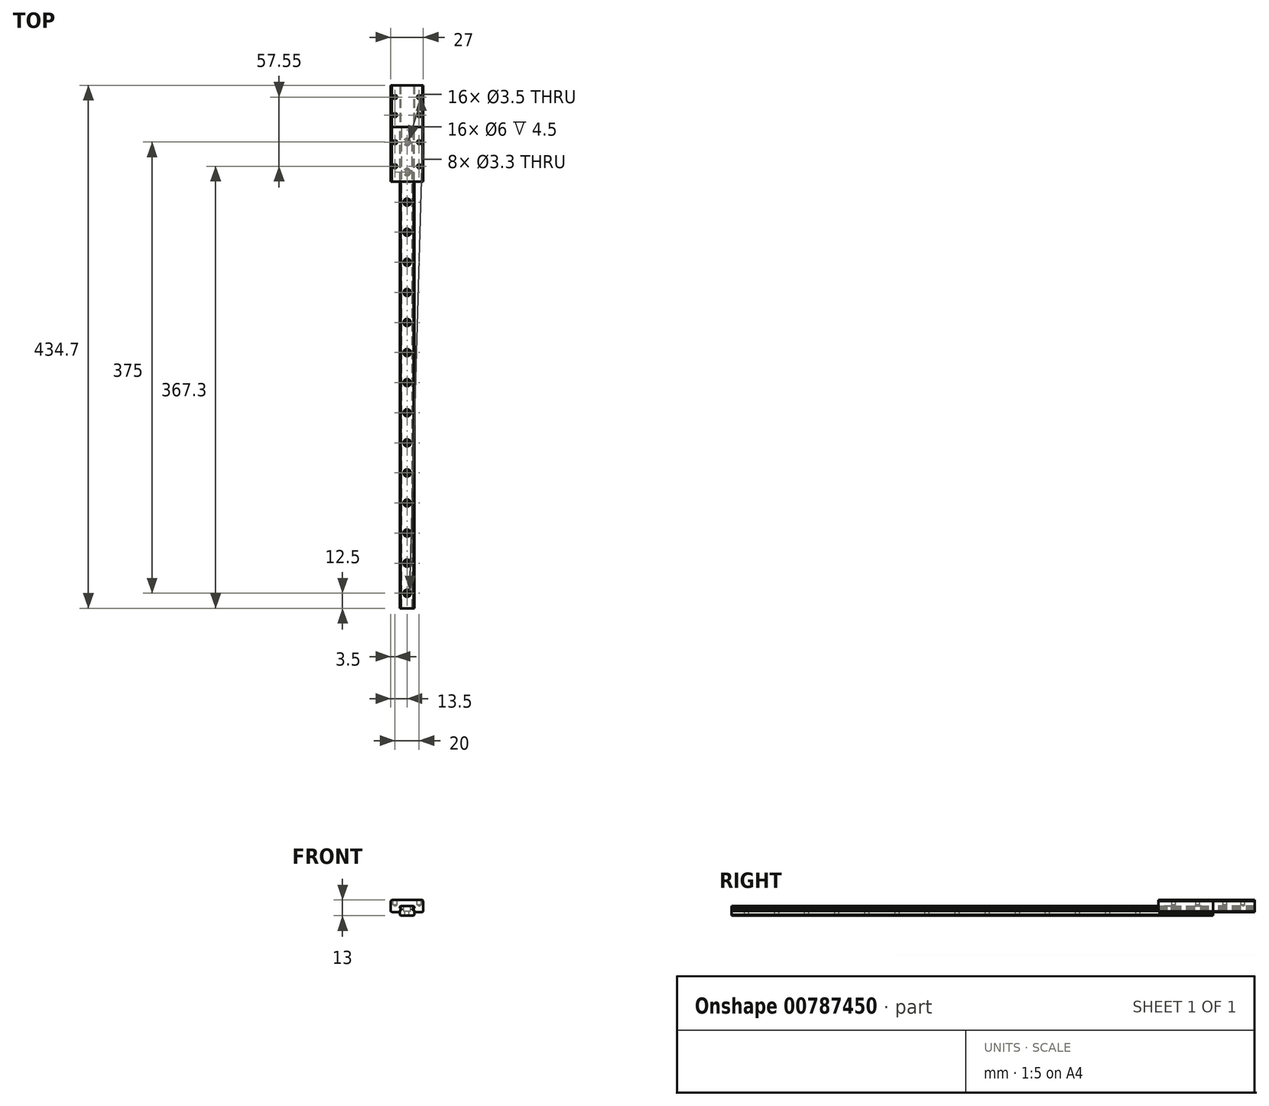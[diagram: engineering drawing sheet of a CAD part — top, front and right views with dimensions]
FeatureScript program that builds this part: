
annotation { "Feature Type Name" : "Feature", "Feature Type Description" : "" }
export const myFeature = defineFeature(function(context is Context, id is Id, definition is map)
    precondition{}
    {
        {
            var Q0;
            Q0=qCreatedBy(makeId("Front.planeOp"),FACE);
            var sketch = newSketch(context, id + "F0", { "sketchPlane" : qUnion([Q0])});
            skLineSegment(sketch, "E0.bottom", {"start": v(5.3, -4) * mm, "end": v(-5.3, -4) * mm});
            skLineSegment(sketch, "E0.top", {"start": v(5.3, 4) * mm, "end": v(-5.3, 4) * mm});
            skLineSegment(sketch, "E0.left", {"start": v(6, -3.3) * mm, "end": v(6, 0.09) * mm});
            skLineSegment(sketch, "E0.right", {"start": v(-6, -3.3) * mm, "end": v(-6, 0.09) * mm});
            skPoint(sketch, "E0.middle", {"position": v(0, 0) * mm});
            skLineSegment(sketch, "E1", {"start": v(0, 12.36) * mm, "end": v(0, -9.73) * mm, "construction": true});
            skLineSegment(sketch, "E2", {"start": v(-6, 2.5) * mm, "end": v(-5.3, 1.8) * mm});
            skLineSegment(sketch, "E3", {"start": v(-5.3, 1.8) * mm, "end": v(-4.3, 1.8) * mm});
            skLineSegment(sketch, "E4", {"start": v(-4.3, 1.8) * mm, "end": v(-4.3, 0.8) * mm});
            skLineSegment(sketch, "E5", {"start": v(-4.3, 0.8) * mm, "end": v(-5.3, 0.8) * mm});
            skLineSegment(sketch, "E6", {"start": v(-5.3, 0.8) * mm, "end": v(-6, 0.09) * mm});
            skLineSegment(sketch, "E7.MirrorCS", {"start": v(4.3, 0.8) * mm, "end": v(5.3, 0.8) * mm});
            skLineSegment(sketch, "E8.MirrorCS", {"start": v(5.3, 0.8) * mm, "end": v(6, 0.09) * mm});
            skLineSegment(sketch, "E9.MirrorCS", {"start": v(4.3, 1.8) * mm, "end": v(4.3, 0.8) * mm});
            skLineSegment(sketch, "E10.MirrorCS", {"start": v(6, 2.5) * mm, "end": v(5.3, 1.8) * mm});
            skLineSegment(sketch, "E11.MirrorCS", {"start": v(5.3, 1.8) * mm, "end": v(4.3, 1.8) * mm});
            skLineSegment(sketch, "E12.trimOffspring", {"start": v(-6, 2.5) * mm, "end": v(-6, 3.3) * mm});
            skLineSegment(sketch, "E13.trimOffspring", {"start": v(6, 2.5) * mm, "end": v(6, 3.3) * mm});
            skLineSegment(sketch, "E14", {"start": v(-6, 3.3) * mm, "end": v(-5.3, 4) * mm});
            skLineSegment(sketch, "E15.MirrorCS", {"start": v(6, 3.3) * mm, "end": v(5.3, 4) * mm});
            skLineSegment(sketch, "E16.MirrorCS", {"start": v(-6, -3.3) * mm, "end": v(-5.3, -4) * mm});
            skLineSegment(sketch, "E17.MirrorCS", {"start": v(6, -3.3) * mm, "end": v(5.3, -4) * mm});
            skPoint(sketch, "E18.orphan", {"position": v(-6, 4) * mm});
            skPoint(sketch, "E19.orphan", {"position": v(6, 4) * mm});
            skPoint(sketch, "E20.orphan", {"position": v(6, -4) * mm});
            skPoint(sketch, "E21.orphan", {"position": v(-6, -4) * mm});
            skSolve(sketch);
        }
        {
            var Q0;
            Q0=makeQuery(id+"F0.imprint","IMPRINT",FACE,{"disambiguationData":[TD([[makeQuery(id+"F0.imprint","IMPRINT",EDGE,{"derivedFrom":sQuery(id+"F0.wireOp",EDGE,"E0.bottom")}),-1.0]])]});
            extrude(context, id + "F1", {"entities" : qUnion([Q0]), "depth" : 400 * mm, "offsetDistance" : 25 * mm});
        }
        {
            var Q0;
            Q0=makeQuery(id+"F1.opExtrude","SWEPT_FACE",FACE,{"disambiguationData":[OSD([sQuery(id+"F0.wireOp",EDGE,"E0.top")])]});
            var sketch = newSketch(context, id + "F2", { "sketchPlane" : qUnion([Q0])});
            skLineSegment(sketch, "E22", {"start": v(0, 4.61) * mm, "end": v(0, -375.08) * mm, "construction": true});
            skCircle(sketch, "E23", {"center": v(0, -12.5) * mm, "radius": 1.75 * mm});
            skCircle(sketch, "E24.1.0.0", {"center": v(0, -37.5) * mm, "radius": 1.75 * mm});
            skCircle(sketch, "E24.2.0.0", {"center": v(0, -62.5) * mm, "radius": 1.75 * mm});
            skCircle(sketch, "E24.3.0.0", {"center": v(0, -87.5) * mm, "radius": 1.75 * mm});
            skCircle(sketch, "E24.4.0.0", {"center": v(0, -112.5) * mm, "radius": 1.75 * mm});
            skCircle(sketch, "E24.5.0.0", {"center": v(0, -137.5) * mm, "radius": 1.75 * mm});
            skCircle(sketch, "E24.6.0.0", {"center": v(0, -162.5) * mm, "radius": 1.75 * mm});
            skCircle(sketch, "E24.7.0.0", {"center": v(0, -187.5) * mm, "radius": 1.75 * mm});
            skCircle(sketch, "E24.8.0.0", {"center": v(0, -212.5) * mm, "radius": 1.75 * mm});
            skLineSegment(sketch, "E24.direction1", {"start": v(0, -12.5) * mm, "end": v(0, -37.5) * mm, "construction": true});
            skCircle(sketch, "E25.0.9.0", {"center": v(0, -237.5) * mm, "radius": 1.75 * mm});
            skCircle(sketch, "E25.0.10.0", {"center": v(0, -262.5) * mm, "radius": 1.75 * mm});
            skCircle(sketch, "E25.0.11.0", {"center": v(0, -287.5) * mm, "radius": 1.75 * mm});
            skCircle(sketch, "E25.0.12.0", {"center": v(0, -312.5) * mm, "radius": 1.75 * mm});
            skCircle(sketch, "E25.0.13.0", {"center": v(0, -337.5) * mm, "radius": 1.75 * mm});
            skCircle(sketch, "E26.0.14.0", {"center": v(0, -362.5) * mm, "radius": 1.75 * mm});
            skCircle(sketch, "E26.0.15.0", {"center": v(0, -387.5) * mm, "radius": 1.75 * mm});
            skSolve(sketch);
        }
        {
            var Q0;
            Q0=qSketchRegion(id+"F2",true);
            extrude(context, id + "F3", {"entities" : qUnion([Q0]), "operationType" : NewBodyOperationType.REMOVE, "endBound" : BoundingType.THROUGH_ALL, "oppositeDirection" : true, "depth" : 25 * mm, "offsetDistance" : 25 * mm});
        }
        {
            var Q0;
            Q0=makeQuery(id+"F1.opExtrude","SWEPT_FACE",FACE,{"disambiguationData":[OSD([sQuery(id+"F0.wireOp",EDGE,"E0.top")])]});
            var sketch = newSketch(context, id + "F4", { "sketchPlane" : qUnion([Q0])});
            skLineSegment(sketch, "E27", {"start": v(0, 167.82) * mm, "end": v(0, -211.88) * mm, "construction": true});
            skCircle(sketch, "E28", {"center": v(0, -12.5) * mm, "radius": 3 * mm});
            skCircle(sketch, "E29.1.0.0", {"center": v(0, -37.5) * mm, "radius": 3 * mm});
            skCircle(sketch, "E29.2.0.0", {"center": v(0, -62.5) * mm, "radius": 3 * mm});
            skCircle(sketch, "E29.3.0.0", {"center": v(0, -87.5) * mm, "radius": 3 * mm});
            skCircle(sketch, "E29.4.0.0", {"center": v(0, -112.5) * mm, "radius": 3 * mm});
            skCircle(sketch, "E29.5.0.0", {"center": v(0, -137.5) * mm, "radius": 3 * mm});
            skCircle(sketch, "E29.6.0.0", {"center": v(0, -162.5) * mm, "radius": 3 * mm});
            skCircle(sketch, "E29.7.0.0", {"center": v(0, -187.5) * mm, "radius": 3 * mm});
            skCircle(sketch, "E29.8.0.0", {"center": v(0, -212.5) * mm, "radius": 3 * mm});
            skLineSegment(sketch, "E29.direction1", {"start": v(0, -12.5) * mm, "end": v(0, -37.5) * mm, "construction": true});
            skCircle(sketch, "E30.0.9.0", {"center": v(0, -237.5) * mm, "radius": 3 * mm});
            skCircle(sketch, "E30.0.10.0", {"center": v(0, -262.5) * mm, "radius": 3 * mm});
            skCircle(sketch, "E30.0.11.0", {"center": v(0, -287.5) * mm, "radius": 3 * mm});
            skCircle(sketch, "E30.0.12.0", {"center": v(0, -312.5) * mm, "radius": 3 * mm});
            skCircle(sketch, "E30.0.13.0", {"center": v(0, -337.5) * mm, "radius": 3 * mm});
            skCircle(sketch, "E31.0.14.0", {"center": v(0, -362.5) * mm, "radius": 3 * mm});
            skCircle(sketch, "E31.0.15.0", {"center": v(0, -387.5) * mm, "radius": 3 * mm});
            skSolve(sketch);
        }
        {
            var Q0;
            Q0 = qSketchRegion(id + "F4", true);
            extrude(context, id + "F5", {"entities" : qUnion([Q0]), "operationType" : NewBodyOperationType.REMOVE, "oppositeDirection" : true, "depth" : 4.5 * mm, "offsetDistance" : 25 * mm});
        }
        {
            var Q0;
            Q0=qCreatedBy(makeId("Front.planeOp"),FACE);
            var sketch = newSketch(context, id + "F6", { "sketchPlane" : qUnion([Q0])});
            skLineSegment(sketch, "E32", {"start": v(-6.15, -1) * mm, "end": v(-12.8, -1) * mm});
            skLineSegment(sketch, "E33", {"start": v(-13.5, -0.3) * mm, "end": v(-13.5, 8.3) * mm});
            skLineSegment(sketch, "E34", {"start": v(-12.8, 9) * mm, "end": v(0, 9) * mm});
            skLineSegment(sketch, "E35", {"start": v(-6.15, -1) * mm, "end": v(-6.15, 0.15) * mm});
            skLineSegment(sketch, "E36", {"start": v(-6.15, 0.15) * mm, "end": v(-5.3, 1) * mm});
            skLineSegment(sketch, "E37", {"start": v(-5.3, 1) * mm, "end": v(-5.3, 1.58) * mm});
            skLineSegment(sketch, "E38", {"start": v(-5.3, 1.58) * mm, "end": v(-6.15, 2.44) * mm});
            skLineSegment(sketch, "E39", {"start": v(-6.15, 2.44) * mm, "end": v(-6.15, 3.36) * mm});
            skLineSegment(sketch, "E40", {"start": v(-6.15, 3.36) * mm, "end": v(-5.36, 4.15) * mm});
            skLineSegment(sketch, "E41", {"start": v(-5.36, 4.15) * mm, "end": v(0, 4.15) * mm});
            skLineSegment(sketch, "E42", {"start": v(-13.5, 8.3) * mm, "end": v(-12.8, 9) * mm});
            skLineSegment(sketch, "E43", {"start": v(-12.8, -1) * mm, "end": v(-13.5, -0.3) * mm});
            skPoint(sketch, "E44.orphan", {"position": v(-13.5, -1) * mm});
            skPoint(sketch, "E45.orphan", {"position": v(-13.5, 9) * mm});
            skLineSegment(sketch, "E46.MirrorCS", {"start": v(12.8, 9) * mm, "end": v(0, 9) * mm});
            skLineSegment(sketch, "E47.MirrorCS", {"start": v(13.5, 8.3) * mm, "end": v(12.8, 9) * mm});
            skLineSegment(sketch, "E48.MirrorCS", {"start": v(13.5, -0.3) * mm, "end": v(13.5, 8.3) * mm});
            skLineSegment(sketch, "E49.MirrorCS", {"start": v(12.8, -1) * mm, "end": v(13.5, -0.3) * mm});
            skLineSegment(sketch, "E50.MirrorCS", {"start": v(6.15, -1) * mm, "end": v(12.8, -1) * mm});
            skLineSegment(sketch, "E51.MirrorCS", {"start": v(6.15, -1) * mm, "end": v(6.15, 0.15) * mm});
            skLineSegment(sketch, "E52.MirrorCS", {"start": v(6.15, 0.15) * mm, "end": v(5.3, 1) * mm});
            skLineSegment(sketch, "E53.MirrorCS", {"start": v(5.3, 1) * mm, "end": v(5.3, 1.58) * mm});
            skLineSegment(sketch, "E54.MirrorCS", {"start": v(5.3, 1.58) * mm, "end": v(6.15, 2.44) * mm});
            skLineSegment(sketch, "E55.MirrorCS", {"start": v(6.15, 2.44) * mm, "end": v(6.15, 3.36) * mm});
            skLineSegment(sketch, "E56.MirrorCS", {"start": v(6.15, 3.36) * mm, "end": v(5.36, 4.15) * mm});
            skLineSegment(sketch, "E57.MirrorCS", {"start": v(5.36, 4.15) * mm, "end": v(0, 4.15) * mm});
            skSolve(sketch);
        }
        {
            var Q0;
            Q0=qSketchRegion(id+"F6",true);
            extrude(context, id + "F7", {"entities" : qUnion([Q0]), "depth" : 45.4 * mm, "offsetDistance" : 25 * mm});
        }
        {
            var Q0;
            Q0=qSketchRegion(id+"F6",true);
            extrude(context, id + "F8", {"entities" : qUnion([Q0]), "oppositeDirection" : true, "depth" : 34.7 * mm, "offsetDistance" : 25 * mm});
        }
        {
            var Q0;
            Q0=makeQuery(id+"F7.opExtrude","SWEPT_FACE",FACE,{"disambiguationData":[OSD([sQuery(id+"F6.wireOp",EDGE,"E34"),sQuery(id+"F6.wireOp",EDGE,"E46.MirrorCS")])]});
            var sketch = newSketch(context, id + "F9", { "sketchPlane" : qUnion([Q0])});
            skLineSegment(sketch, "E58", {"start": v(-12.8, 0) * mm, "end": v(12.8, -45.4) * mm, "construction": true});
            skLineSegment(sketch, "E59", {"start": v(12.8, 0) * mm, "end": v(-12.8, -45.4) * mm, "construction": true});
            skLineSegment(sketch, "E60", {"start": v(-37.81, -22.7) * mm, "end": v(32.35, -22.7) * mm, "construction": true});
            skPoint(sketch, "E60.startSnap0", {"position": v(0, -22.7) * mm});
            skLineSegment(sketch, "E61", {"start": v(0, 0) * mm, "end": v(0, -61.52) * mm, "construction": true});
            skCircle(sketch, "E62", {"center": v(-10, -12.7) * mm, "radius": 1.5 * mm});
            skCircle(sketch, "E63.MirrorC", {"center": v(10, -12.7) * mm, "radius": 1.5 * mm});
            skCircle(sketch, "E64.MirrorC", {"center": v(-10, -32.7) * mm, "radius": 1.5 * mm});
            skCircle(sketch, "E65.MirrorC", {"center": v(10, -32.7) * mm, "radius": 1.5 * mm});
            skSolve(sketch);
        }
        {
            var Q0;
            Q0=makeQuery(id+"F8.opExtrude","SWEPT_FACE",FACE,{"disambiguationData":[OSD([sQuery(id+"F6.wireOp",EDGE,"E34"),sQuery(id+"F6.wireOp",EDGE,"E46.MirrorCS")])]});
            var sketch = newSketch(context, id + "F10", { "sketchPlane" : qUnion([Q0])});
            skLineSegment(sketch, "E66", {"start": v(-34.35, 17.35) * mm, "end": v(28.23, 17.35) * mm, "construction": true});
            skLineSegment(sketch, "E67", {"start": v(0, 49.38) * mm, "end": v(0, -1.77) * mm, "construction": true});
            skCircle(sketch, "E68", {"center": v(-10, 24.85) * mm, "radius": 1.5 * mm});
            skCircle(sketch, "E69.MirrorC", {"center": v(10, 24.85) * mm, "radius": 1.5 * mm});
            skCircle(sketch, "E70.MirrorC", {"center": v(-10, 9.85) * mm, "radius": 1.5 * mm});
            skCircle(sketch, "E71.MirrorC", {"center": v(10, 9.85) * mm, "radius": 1.5 * mm});
            skSolve(sketch);
        }
        {
            var Q0;
            Q0=sQuery(id+"F9.wireOp",VERTEX,"E62.center");
            var Q1;
            Q1=sQuery(id+"F9.wireOp",VERTEX,"E63.MirrorC.center");
            var Q2;
            Q2=sQuery(id+"F9.wireOp",VERTEX,"E64.MirrorC.center");
            var Q3;
            Q3=sQuery(id+"F9.wireOp",VERTEX,"E65.MirrorC.center");
            var Q4;
            Q4=makeQuery(id+"F7.opExtrude","SWEPT_BODY",BODY,{"disambiguationData":[OSD([sQuery(id+"F6.wireOp",EDGE,"E32"),sQuery(id+"F6.wireOp",EDGE,"E33"),sQuery(id+"F6.wireOp",EDGE,"E34"),sQuery(id+"F6.wireOp",EDGE,"E35"),sQuery(id+"F6.wireOp",EDGE,"E36"),sQuery(id+"F6.wireOp",EDGE,"E37"),sQuery(id+"F6.wireOp",EDGE,"E38"),sQuery(id+"F6.wireOp",EDGE,"E39"),sQuery(id+"F6.wireOp",EDGE,"E40"),sQuery(id+"F6.wireOp",EDGE,"E41"),sQuery(id+"F6.wireOp",EDGE,"E42"),sQuery(id+"F6.wireOp",EDGE,"E43"),sQuery(id+"F6.wireOp",EDGE,"E46.MirrorCS"),sQuery(id+"F6.wireOp",EDGE,"E47.MirrorCS"),sQuery(id+"F6.wireOp",EDGE,"E48.MirrorCS"),sQuery(id+"F6.wireOp",EDGE,"E49.MirrorCS"),sQuery(id+"F6.wireOp",EDGE,"E50.MirrorCS"),sQuery(id+"F6.wireOp",EDGE,"E51.MirrorCS"),sQuery(id+"F6.wireOp",EDGE,"E52.MirrorCS"),sQuery(id+"F6.wireOp",EDGE,"E53.MirrorCS"),sQuery(id+"F6.wireOp",EDGE,"E54.MirrorCS"),sQuery(id+"F6.wireOp",EDGE,"E55.MirrorCS"),sQuery(id+"F6.wireOp",EDGE,"E56.MirrorCS"),sQuery(id+"F6.wireOp",EDGE,"E57.MirrorCS")])]});
            hole(context, id + "F11", {"style" : HoleStyle.SIMPLE, "endStyle" : HoleEndStyle.BLIND, "standardTappedOrClearance" : lookupTablePath({ "standard" : "ISO", "fit" : "Normal", "size" : "M3", "type" : "Clearance" }), "standardBlindInLast" : lookupTablePath({ "fit" : "Standard", "standard" : "ISO", "size" : "M3", "type" : "Clearance" }), "holeDiameter" : 3.3 * mm, "majorDiameter" : 5 * mm, "holeDepth" : 4 * mm, "isTappedThrough" : true, "tappedDepth" : 12 * mm, "tapClearance" : 3, "startFromSketch" : true, "locations" : qUnion([Q0, Q1, Q2, Q3]), "scope" : qUnion([Q4])});
        }
        {
            var Q0;
            Q0=sQuery(id+"F10.wireOp",VERTEX,"E68.center");
            var Q1;
            Q1=sQuery(id+"F10.wireOp",VERTEX,"E69.MirrorC.center");
            var Q2;
            Q2=sQuery(id+"F10.wireOp",VERTEX,"E71.MirrorC.center");
            var Q3;
            Q3=sQuery(id+"F10.wireOp",VERTEX,"E70.MirrorC.center");
            var Q4;
            Q4=makeQuery(id+"F8.opExtrude","SWEPT_BODY",BODY,{"disambiguationData":[OSD([sQuery(id+"F6.wireOp",EDGE,"E32"),sQuery(id+"F6.wireOp",EDGE,"E33"),sQuery(id+"F6.wireOp",EDGE,"E34"),sQuery(id+"F6.wireOp",EDGE,"E35"),sQuery(id+"F6.wireOp",EDGE,"E36"),sQuery(id+"F6.wireOp",EDGE,"E37"),sQuery(id+"F6.wireOp",EDGE,"E38"),sQuery(id+"F6.wireOp",EDGE,"E39"),sQuery(id+"F6.wireOp",EDGE,"E40"),sQuery(id+"F6.wireOp",EDGE,"E41"),sQuery(id+"F6.wireOp",EDGE,"E42"),sQuery(id+"F6.wireOp",EDGE,"E43"),sQuery(id+"F6.wireOp",EDGE,"E46.MirrorCS"),sQuery(id+"F6.wireOp",EDGE,"E47.MirrorCS"),sQuery(id+"F6.wireOp",EDGE,"E48.MirrorCS"),sQuery(id+"F6.wireOp",EDGE,"E49.MirrorCS"),sQuery(id+"F6.wireOp",EDGE,"E50.MirrorCS"),sQuery(id+"F6.wireOp",EDGE,"E51.MirrorCS"),sQuery(id+"F6.wireOp",EDGE,"E52.MirrorCS"),sQuery(id+"F6.wireOp",EDGE,"E53.MirrorCS"),sQuery(id+"F6.wireOp",EDGE,"E54.MirrorCS"),sQuery(id+"F6.wireOp",EDGE,"E55.MirrorCS"),sQuery(id+"F6.wireOp",EDGE,"E56.MirrorCS"),sQuery(id+"F6.wireOp",EDGE,"E57.MirrorCS")])]});
            hole(context, id + "F12", {"style" : HoleStyle.SIMPLE, "endStyle" : HoleEndStyle.BLIND, "standardTappedOrClearance" : lookupTablePath({ "standard" : "ISO", "fit" : "Normal", "size" : "M3", "type" : "Clearance" }), "standardBlindInLast" : lookupTablePath({ "fit" : "Standard", "standard" : "ISO", "size" : "M3", "type" : "Clearance" }), "holeDiameter" : 3.3 * mm, "majorDiameter" : 5 * mm, "holeDepth" : 4 * mm, "isTappedThrough" : true, "tappedDepth" : 12 * mm, "tapClearance" : 3, "startFromSketch" : true, "locations" : qUnion([Q0, Q1, Q2, Q3]), "scope" : qUnion([Q4])});
        }
    });
